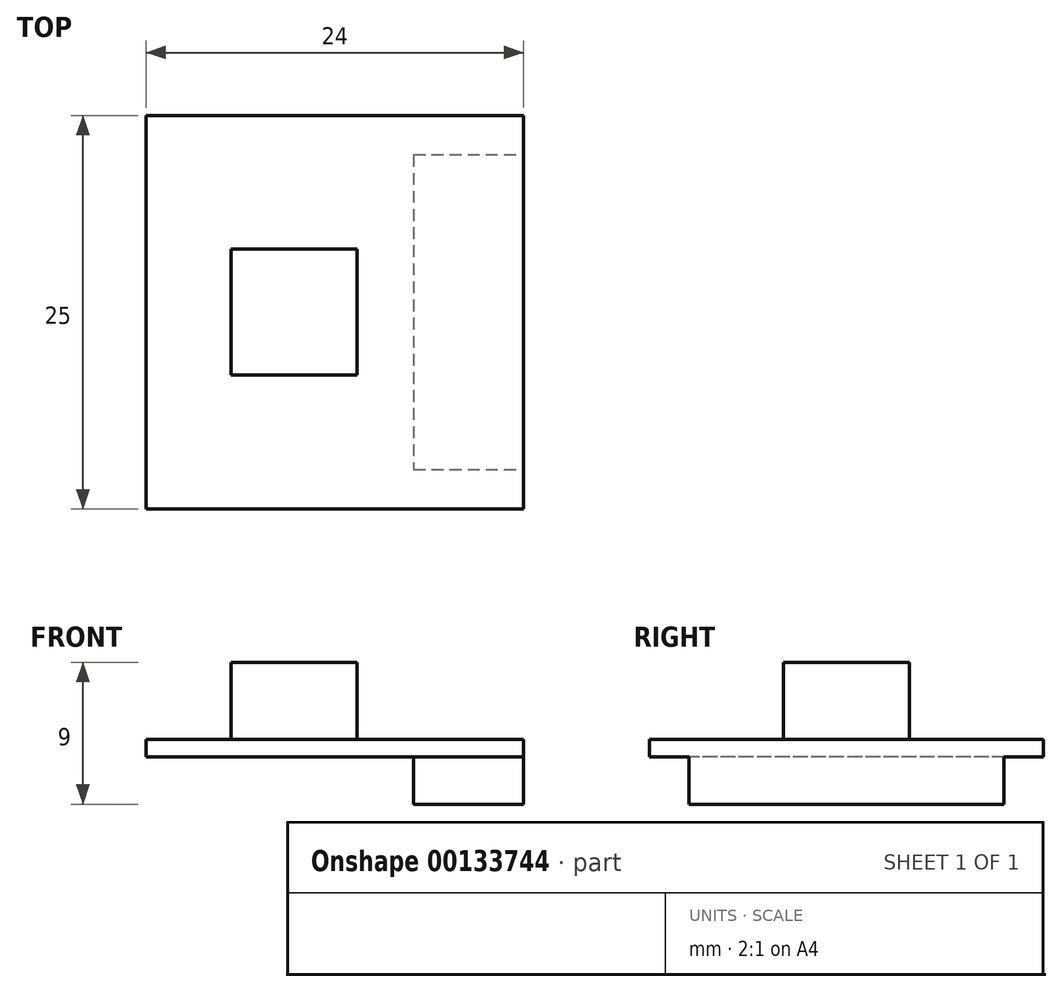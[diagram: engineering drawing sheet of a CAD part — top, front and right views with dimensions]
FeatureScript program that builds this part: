
annotation { "Feature Type Name" : "Feature", "Feature Type Description" : "" }
export const myFeature = defineFeature(function(context is Context, id is Id, definition is map)
    precondition{}
    {
        {
            var Q0;
            Q0=qCreatedBy(makeId("Top.planeOp"),FACE);
            var sketch = newSketch(context, id + "F0", { "sketchPlane" : qUnion([Q0])});
            skLineSegment(sketch, "E0.bottom", {"start": v(-12, 12.5) * mm, "end": v(12, 12.5) * mm});
            skLineSegment(sketch, "E0.top", {"start": v(-12, -12.5) * mm, "end": v(12, -12.5) * mm});
            skLineSegment(sketch, "E0.left", {"start": v(-12, 12.5) * mm, "end": v(-12, -12.5) * mm});
            skLineSegment(sketch, "E0.right", {"start": v(12, 12.5) * mm, "end": v(12, -12.5) * mm});
            skLineSegment(sketch, "E1.bottom", {"start": v(-6.6, 4) * mm, "end": v(1.4, 4) * mm});
            skLineSegment(sketch, "E1.top", {"start": v(-6.6, -4) * mm, "end": v(1.4, -4) * mm});
            skLineSegment(sketch, "E1.left", {"start": v(-6.6, 4) * mm, "end": v(-6.6, -4) * mm});
            skLineSegment(sketch, "E1.right", {"start": v(1.4, 4) * mm, "end": v(1.4, -4) * mm});
            skLineSegment(sketch, "E2.bottom", {"start": v(5, 10) * mm, "end": v(12, 10) * mm});
            skLineSegment(sketch, "E2.top", {"start": v(5, -10) * mm, "end": v(12, -10) * mm});
            skLineSegment(sketch, "E2.left", {"start": v(5, 10) * mm, "end": v(5, -10) * mm});
            skLineSegment(sketch, "E2.right", {"start": v(12, 10) * mm, "end": v(12, -10) * mm});
            skPoint(sketch, "E3", {"position": v(0, 12.5) * mm});
            skPoint(sketch, "E4", {"position": v(5, 0) * mm});
            skPoint(sketch, "E5", {"position": v(-12, 0) * mm});
            skPoint(sketch, "E6", {"position": v(-6.6, 0) * mm});
            skSolve(sketch);
        }
        {
            var Q0;
            {var subQ0=sQuery(id+"F0.wireOp",EDGE,"E0.bottom");Q0=makeQuery(id+"F0.imprint","IMPRINT",FACE,{"disambiguationData":[TD([[makeQuery(id+"F0.imprint","IMPRINT",EDGE,{"derivedFrom":subQ0}),-1.0]])]});}
            var Q1;
            Q1=makeQuery(id+"F0.imprint","IMPRINT",FACE,{"disambiguationData":[TD([[makeQuery(id+"F0.imprint","IMPRINT",EDGE,{"derivedFrom":sQuery(id+"F0.wireOp",EDGE,"E1.bottom")}),-1.0]])]});
            var Q2;
            Q2=makeQuery(id+"F0.imprint","IMPRINT",FACE,{"disambiguationData":[TD([[makeQuery(id+"F0.imprint","IMPRINT",EDGE,{"derivedFrom":sQuery(id+"F0.wireOp",EDGE,"E2.bottom")}),-1.0]])]});
            extrude(context, id + "F1", {"entities" : qUnion([Q0, Q1, Q2]), "depth" : 1.1 * mm});
        }
        {
            var Q0;
            Q0=makeQuery(id+"F0.imprint","IMPRINT",FACE,{"disambiguationData":[TD([[makeQuery(id+"F0.imprint","IMPRINT",EDGE,{"derivedFrom":sQuery(id+"F0.wireOp",EDGE,"E1.bottom")}),-1.0]])]});
            extrude(context, id + "F2", {"entities" : qUnion([Q0]), "operationType" : NewBodyOperationType.ADD, "depth" : 6 * mm});
        }
        {
            var Q0;
            Q0=makeQuery(id+"F0.imprint","IMPRINT",FACE,{"disambiguationData":[TD([[makeQuery(id+"F0.imprint","IMPRINT",EDGE,{"derivedFrom":sQuery(id+"F0.wireOp",EDGE,"E2.bottom")}),-1.0]])]});
            extrude(context, id + "F3", {"entities" : qUnion([Q0]), "operationType" : NewBodyOperationType.ADD, "oppositeDirection" : true, "depth" : 3 * mm});
        }
    });
